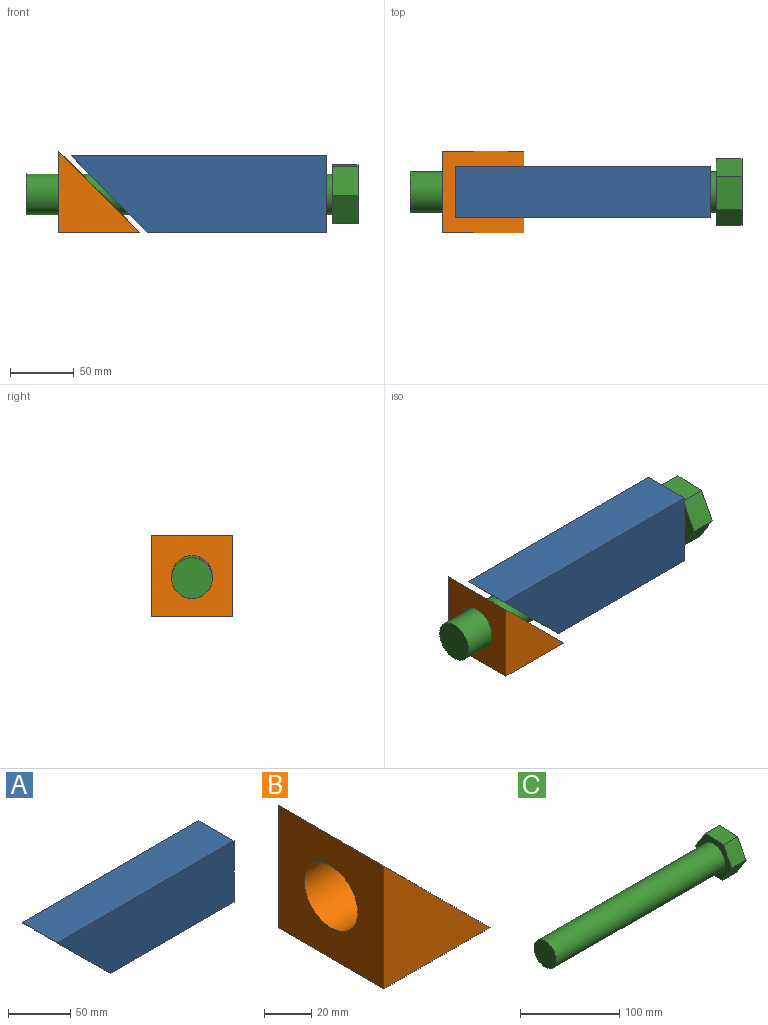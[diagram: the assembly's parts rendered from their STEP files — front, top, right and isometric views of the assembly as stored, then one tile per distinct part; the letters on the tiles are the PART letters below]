
ASSEMBLY  parts=3 mates=2
PART A: 10 faces, bbox 200x40x60 mm
  f0: plane 200x60mm, normal (0,1,0), area 10200mm2, adj f6,f7,f8,f9
  f1: plane 200x60mm, normal (0,-1,0), area 10200mm2, adj f6,f7,f8,f9
  f2: plane 196x52mm, normal (0,-1,0), area 8840mm2, adj f3,f5,f8,f9
  f3: plane 144x32mm, normal (0,0,1), area 4608mm2, adj f2,f4,f8,f9
  f4: plane 196x52mm, normal (0,1,0), area 8840mm2, adj f3,f5,f8,f9
  f5: plane 196x32mm, normal (0,0,-1), area 6272mm2, adj f2,f4,f8,f9
  f6: plane 140x40mm, normal (0,0,-1), area 5600mm2, adj f0,f1,f8,f9
  f7: plane 200x40mm, normal (0,0,1), area 8000mm2, adj f0,f1,f8,f9
  f8: plane 60x40mm, normal (1,0,0), area 736mm2, adj f0,f1,f2,f3,f4,f5,f6,f7
  f9: plane 60x60mm, normal (-0.71,0,-0.71), area 1040.9mm2, adj f0,f1,f2,f3,f4,f5,f6,f7
PART B: 6 faces, bbox 63.5x63.5x63.5 mm
  f0: plane 63.5x63.5mm, normal (0,-1,0), area 2016.1mm2, adj f2,f3,f5
  f1: plane 63.5x63.5mm, normal (0,1,0), area 2016.1mm2, adj f2,f3,f5
  f2: plane 63.5x63.5mm, normal (-1,0,0), area 3228mm2, adj f0,f1,f3,f4,f5
  f3: plane 63.5x63.5mm, normal (0,0,-1), area 4032.3mm2, adj f0,f1,f2,f5
  f4: cylinder r=16mm len=47.76mm, axis (1,0,0), area 3191.9mm2, adj f2,f5
  f5: plane 63.5x63.5mm, normal (0.71,0,0.71), area 4565.1mm2, adj f0,f1,f2,f3,f4
PART C: 10 faces, bbox 260x51.9x46 mm
  f0: cylinder r=16mm len=240mm, axis (-1,0,0), area 24127.4mm2, adj f1,f9
  f1: plane 32x32mm, normal (-1,0,0), area 804.2mm2, adj f0
  f2: plane 25.96x20mm, normal (0,0.04,-1), area 519.6mm2, adj f3,f7,f8,f9
  f3: plane 23x20mm, normal (0,0.89,-0.46), area 519.6mm2, adj f2,f4,f8,f9
  f4: plane 21.96x20mm, normal (0,0.85,0.53), area 519.6mm2, adj f3,f5,f8,f9
  f5: plane 25.96x20mm, normal (0,-0.04,1), area 519.6mm2, adj f4,f6,f8,f9
  f6: plane 23x20mm, normal (0,-0.89,0.46), area 519.6mm2, adj f5,f7,f8,f9
  f7: plane 21.96x20mm, normal (0,-0.85,-0.53), area 519.6mm2, adj f2,f6,f8,f9
  f8: plane 51.92x46mm, normal (1,0,0), area 1753.7mm2, adj f2,f3,f4,f5,f6,f7
  f9: plane 51.92x46mm, normal (-1,0,0), area 949.5mm2, adj f0,f2,f3,f4,f5,f6,f7
PLACE A t=(-130,0,30)mm
PLACE B t=(-108.05,0,0)mm
PLACE C t=(-165.48,0,30)mm
MATE slider B.f4 <-> A.f8  axis (-1,0,0) through (-139.8,0,31.75)mm
MATE slider A.f8 <-> C.f0  axis (1,0,0) through (70,0,30)mm
